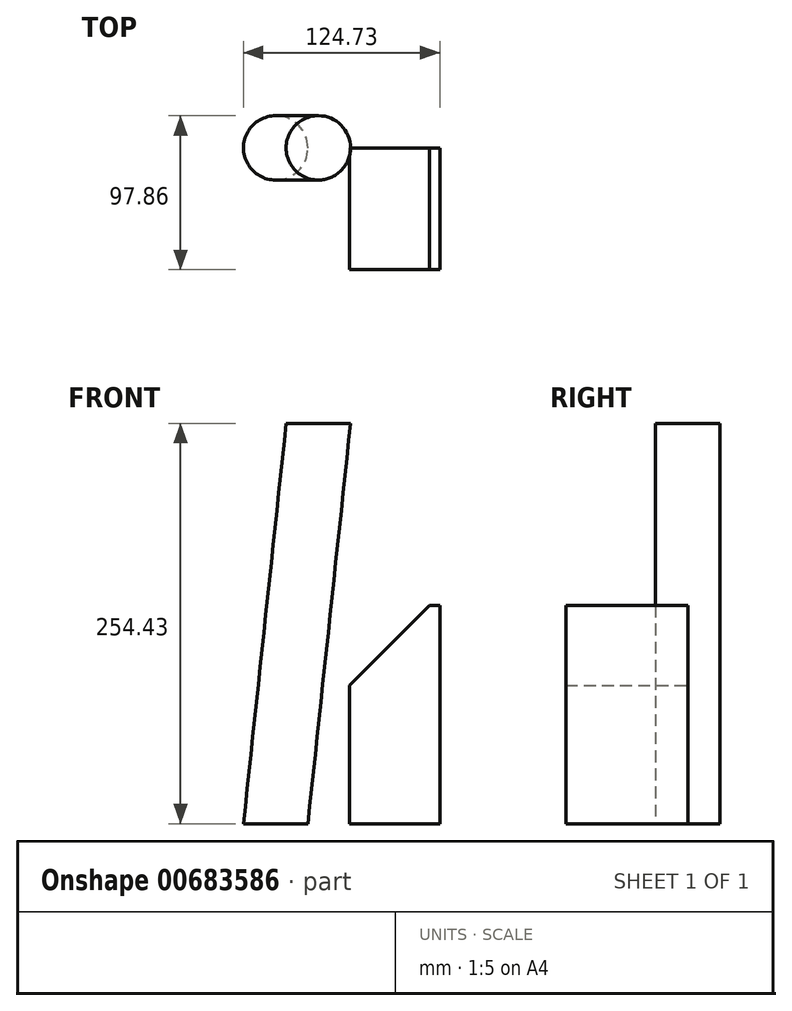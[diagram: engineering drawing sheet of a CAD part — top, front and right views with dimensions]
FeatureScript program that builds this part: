
annotation { "Feature Type Name" : "Feature", "Feature Type Description" : "" }
export const myFeature = defineFeature(function(context is Context, id is Id, definition is map)
    precondition{}
    {
        {
            var Q0;
            Q0=qCreatedBy(makeId("Top.planeOp"),FACE);
            var sketch = newSketch(context, id + "F0", { "sketchPlane" : qUnion([Q0])});
            skLineSegment(sketch, "E0.bottom", {"start": v(0, 0) * mm, "end": v(57.48, 0) * mm});
            skLineSegment(sketch, "E0.top", {"start": v(0, -77.4) * mm, "end": v(57.48, -77.4) * mm});
            skLineSegment(sketch, "E0.left", {"start": v(0, 0) * mm, "end": v(0, -77.4) * mm});
            skLineSegment(sketch, "E0.right", {"start": v(57.48, 0) * mm, "end": v(57.48, -77.4) * mm});
            skSolve(sketch);
        }
        {
            var Q0;
            Q0 = qSketchRegion(id + "F0", true);
            extrude(context, id + "F1", {"entities" : qUnion([Q0]), "depth" : 138.62 * mm, "offsetDistance" : 25.4 * mm});
        }
        {
            var Q0;
            Q0=makeQuery(id+"F1.opExtrude","CAP_EDGE",EDGE,{"disambiguationData":[OSD([sQuery(id+"F0.wireOp",EDGE,"E0.left")])],"isStart":false});
            chamfer(context, id + "F2", {"entities" : qUnion([Q0]), "width" : 50.8 * mm, "tangentPropagation" : true});
        }
        {
            var Q0;
            Q0=qCreatedBy(makeId("Top.planeOp"),FACE);
            var sketch = newSketch(context, id + "F3", { "sketchPlane" : qUnion([Q0])});
            skCircle(sketch, "E1", {"center": v(-46.8, 0) * mm, "radius": 20.45 * mm});
            skSolve(sketch);
        }
        {
            var Q0;
            Q0=qCreatedBy(makeId("Front.planeOp"),FACE);
            var sketch = newSketch(context, id + "F4", { "sketchPlane" : qUnion([Q0])});
            skLineSegment(sketch, "E2", {"start": v(-49.22, 0) * mm, "end": v(-22.13, 254.43) * mm});
            skSolve(sketch);
        }
        {
            var Q0;
            Q0=makeQuery(id+"F3.imprint","IMPRINT",FACE,{"disambiguationData":[TD([[makeQuery(id+"F3.imprint","IMPRINT",EDGE,{"derivedFrom":sQuery(id+"F3.wireOp",EDGE,"E1")}),1.0]])]});
            var Q1;
            Q1=sQuery(id+"F4.wireOp",EDGE,"E2");
            sweep(context, id + "F5", {"profiles" : qUnion([Q0]), "path" : qUnion([Q1])});
        }
    });
